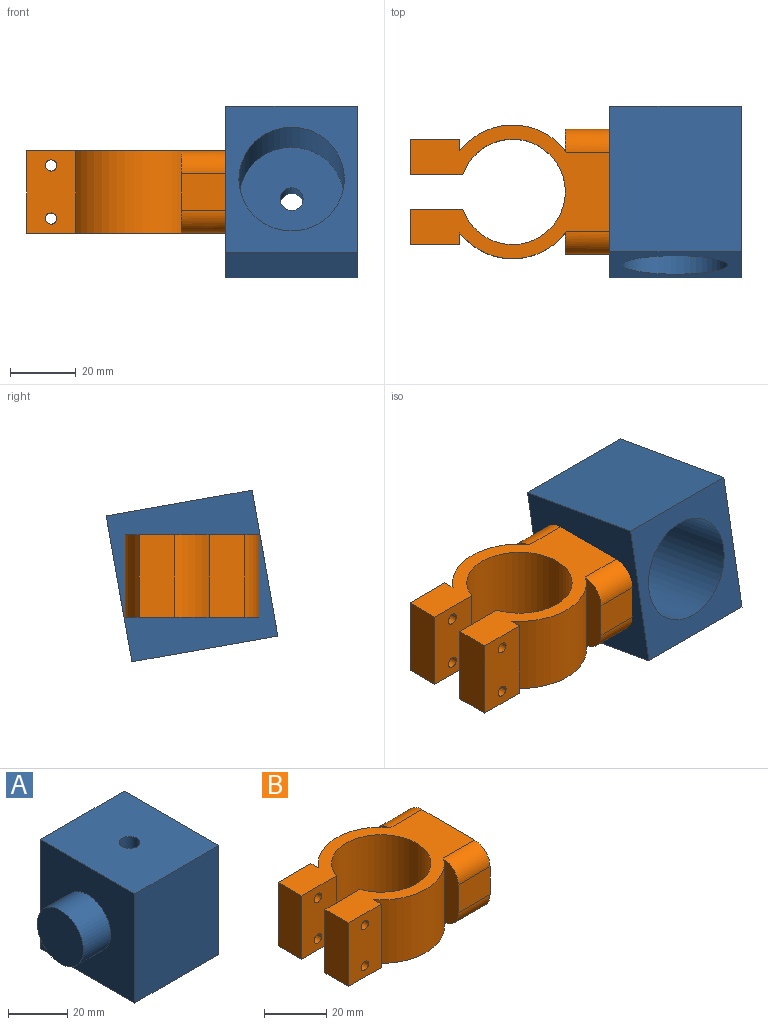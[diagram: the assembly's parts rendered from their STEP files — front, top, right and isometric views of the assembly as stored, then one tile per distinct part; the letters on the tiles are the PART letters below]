
ASSEMBLY  parts=2 mates=1
PART A: 11 faces, bbox 53x45x45 mm
  f0: cylinder r=11mm len=22mm, axis (-1,0,0), area 898.5mm2, adj f1,f7
  f1: plane 22x22mm, normal (-1,0,0), area 380.1mm2, adj f0
  f2: plane 45x40mm, normal (0,0,-1), area 995.8mm2, adj f3,f5,f6,f7,f8
  f3: plane 45x40mm, normal (0,1,0), area 1800mm2, adj f2,f4,f6,f7
  f4: plane 45x40mm, normal (0,0,1), area 1761.5mm2, adj f3,f5,f6,f7,f10
  f5: plane 45x40mm, normal (0,-1,0), area 1800mm2, adj f2,f4,f6,f7
  f6: plane 45x45mm, normal (1,0,0), area 2025mm2, adj f2,f3,f4,f5
  f7: plane 45x45mm, normal (-1,0,0), area 1644.9mm2, adj f0,f2,f3,f4,f5
  f8: cylinder r=16mm len=35mm, axis (0,0,-1), area 3518.6mm2, adj f2,f9
  f9: plane 32x32mm, normal (0,0,-1), area 765.8mm2, adj f8,f10
  f10: cylinder r=3.5mm len=10mm, axis (0,0,-1), area 219.9mm2, adj f4,f9
PART B: 42 faces, bbox 61.5x40.6x25 mm
  f0: plane 25x14.96mm, normal (0,1,0), area 319.1mm2, adj f4,f5,f18,f19,f22,f23,f24,f25
  f1: cylinder r=1.7mm len=7.69mm, axis (0,1,0), area 82.1mm2, adj f6,f35
  f2: cylinder r=1.7mm len=7.69mm, axis (0,1,0), area 82.1mm2, adj f6,f28
  f3: cylinder r=20.32mm len=32.44mm, axis (0,0,-1), area 922.3mm2, adj f4,f17,f18,f19,f39,f41
  f4: plane 25x3.52mm, normal (1,0,0), area 88.1mm2, adj f0,f3,f18,f19
  f5: plane 25x10.69mm, normal (-1,0,0), area 267.2mm2, adj f0,f6,f18,f19
  f6: plane 25x15.9mm, normal (0,-1,0), area 379.4mm2, adj f1,f2,f5,f7,f18,f19
  f7: cylinder r=16mm len=32mm, axis (0,0,-1), area 2240.9mm2, adj f6,f8,f18,f19
  f8: plane 25x15.91mm, normal (0,1,0), area 379.7mm2, adj f7,f9,f18,f19,f20,f21
  f9: plane 25x10.69mm, normal (-1,0,0), area 267.1mm2, adj f8,f10,f18,f19
  f10: plane 25x14.96mm, normal (0,-1,0), area 355.8mm2, adj f9,f11,f18,f19,f20,f21
  f11: plane 25x3.56mm, normal (1,0,0), area 88.9mm2, adj f10,f12,f18,f19
  f12: cylinder r=20.32mm len=32.42mm, axis (0,0,-1), area 922.3mm2, adj f11,f13,f18,f19,f38,f40
  f13: plane 24.96x6.49mm, normal (-1,0,0), area 141.2mm2, adj f12,f14,f38,f40
  f14: plane 14.5x11mm, normal (0,-1,0), area 159.5mm2, adj f13,f15,f38,f40
  f15: plane 38x25mm, normal (1,0,0), area 492.5mm2, adj f14,f16,f18,f19,f36,f38,f39,f40
  f16: plane 14.5x11mm, normal (0,1,0), area 159.5mm2, adj f15,f17,f39,f41
  f17: plane 24.96x6.46mm, normal (-1,0,0), area 140.4mm2, adj f3,f16,f39,f41
  f18: plane 61.49x40.64mm, normal (0,0,1), area 1010.4mm2, adj f0,f3,f4,f5,f6,f7,f8,f9
  f19: plane 61.49x40.64mm, normal (0,0,-1), area 1010.4mm2, adj f0,f3,f4,f5,f6,f7,f8,f9
  f20: cylinder r=1.7mm len=10.69mm, axis (0,1,0), area 114.1mm2, adj f8,f10
  f21: cylinder r=1.7mm len=10.69mm, axis (0,1,0), area 114.1mm2, adj f8,f10
  f22: plane 3.25x3mm, normal (0,0,1), area 9.7mm2, adj f0,f23,f27,f28
  f23: plane 3x2.81mm, normal (0.87,0,0.5), area 9.7mm2, adj f0,f22,f24,f28
  f24: plane 3x2.81mm, normal (0.87,0,-0.5), area 9.7mm2, adj f0,f23,f25,f28
  f25: plane 3.25x3mm, normal (0,0,-1), area 9.7mm2, adj f0,f24,f26,f28
  f26: plane 3x2.81mm, normal (-0.87,0,-0.5), area 9.7mm2, adj f0,f25,f27,f28
  f27: plane 3x2.81mm, normal (-0.87,0,0.5), area 9.7mm2, adj f0,f22,f26,f28
  f28: plane 6.5x5.63mm, normal (0,1,0), area 18.4mm2, adj f2,f22,f23,f24,f25,f26,f27
  f29: plane 3.25x3mm, normal (0,0,1), area 9.7mm2, adj f0,f30,f34,f35
  f30: plane 3x2.81mm, normal (0.87,0,0.5), area 9.7mm2, adj f0,f29,f31,f35
  f31: plane 3x2.81mm, normal (0.87,0,-0.5), area 9.7mm2, adj f0,f30,f32,f35
  f32: plane 3.25x3mm, normal (0,0,-1), area 9.7mm2, adj f0,f31,f33,f35
  f33: plane 3x2.81mm, normal (-0.87,0,-0.5), area 9.7mm2, adj f0,f32,f34,f35
  f34: plane 3x2.81mm, normal (-0.87,0,0.5), area 9.7mm2, adj f0,f29,f33,f35
  f35: plane 6.5x5.63mm, normal (0,1,0), area 18.4mm2, adj f1,f29,f30,f31,f32,f33,f34
  f36: cylinder r=11.5mm len=23mm, axis (1,0,0), area 1011.6mm2, adj f15,f37
  f37: plane 23x23mm, normal (1,0,0), area 415.5mm2, adj f36
  f38: cylinder r=7mm len=14.5mm, axis (1,0,0), area 159.3mm2, adj f12,f13,f14,f15,f19
  f39: cylinder r=7mm len=14.5mm, axis (-1,0,0), area 159.3mm2, adj f3,f15,f16,f17,f19
  f40: cylinder r=7mm len=14.5mm, axis (-1,0,0), area 159.3mm2, adj f12,f13,f14,f15,f18
  f41: cylinder r=7mm len=14.5mm, axis (1,0,0), area 159.3mm2, adj f3,f15,f16,f17,f18
PLACE A rot(axis=(-1,0,0),100deg) t=(21.04,56.41,2.55)mm
PLACE B t=(24.2,0,0)mm
MATE cylindrical A.f0 <-> B.f36  axis (-1,0,0) through (21.04,0,12.5)mm
